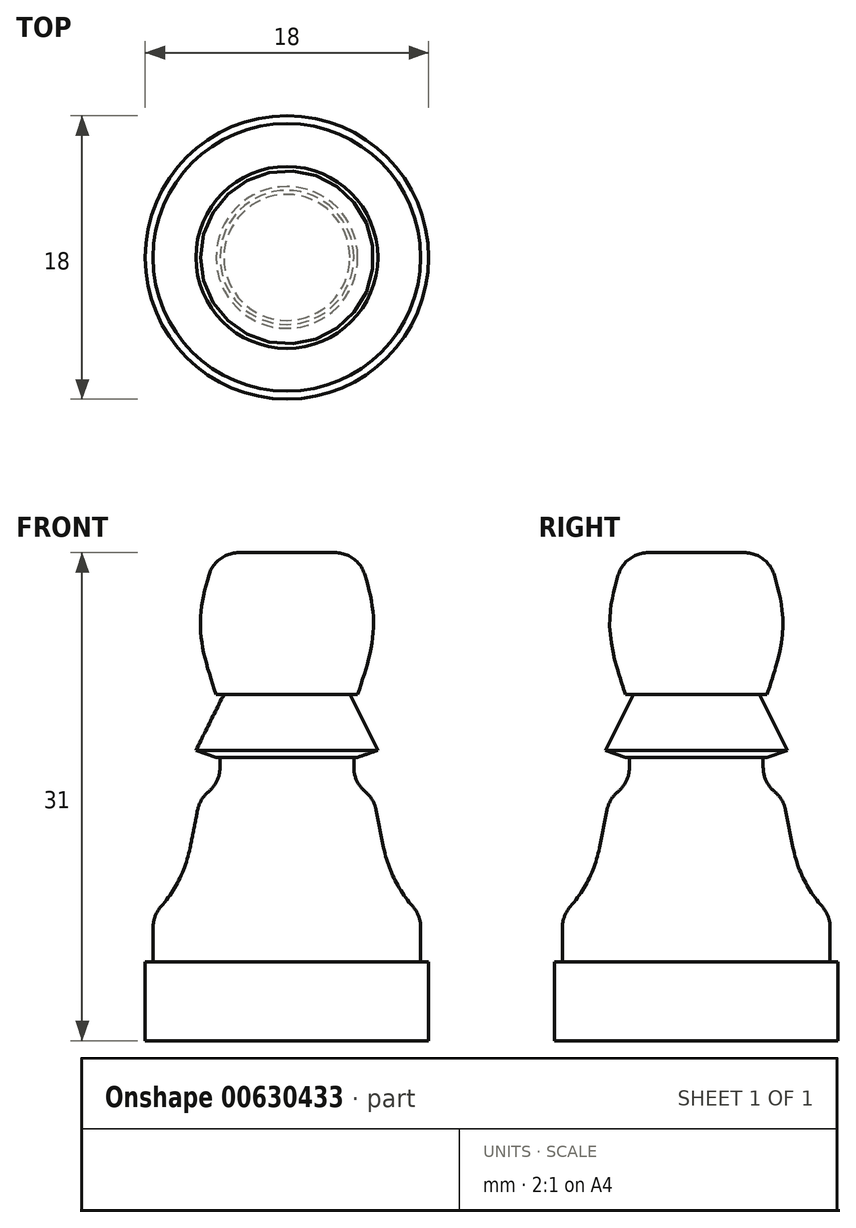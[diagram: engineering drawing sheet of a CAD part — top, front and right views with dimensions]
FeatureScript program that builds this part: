
annotation { "Feature Type Name" : "Feature", "Feature Type Description" : "" }
export const myFeature = defineFeature(function(context is Context, id is Id, definition is map)
    precondition{}
    {
        {
            var Q0;
            Q0=qCreatedBy(makeId("Front.planeOp"),FACE);
            var sketch = newSketch(context, id + "F0", { "sketchPlane" : qUnion([Q0])});
            skLineSegment(sketch, "E0", {"start": v(0, 0) * mm, "end": v(9, 0) * mm});
            skLineSegment(sketch, "E1", {"start": v(0, 0) * mm, "end": v(0, 31) * mm});
            skLineSegment(sketch, "E2", {"start": v(6, 18) * mm, "end": v(4.25, 18) * mm});
            skLineSegment(sketch, "E3", {"start": v(4.25, 18) * mm, "end": v(4.25, 15.5) * mm});
            skPoint(sketch, "E4.orphan", {"position": v(0, 15.5) * mm});
            skLineSegment(sketch, "E5", {"start": v(9, 0) * mm, "end": v(9, 5) * mm});
            skLineSegment(sketch, "E6", {"start": v(9, 5) * mm, "end": v(8.5, 5) * mm});
            skLineSegment(sketch, "E7", {"start": v(8.5, 5) * mm, "end": v(8.5, 8) * mm});
            skLineSegment(sketch, "E8", {"start": v(8.5, 8) * mm, "end": v(7, 8) * mm});
            skLineSegment(sketch, "E9", {"start": v(0, 31) * mm, "end": v(4.5, 31) * mm});
            skFitSpline(sketch, "E10", {"points": [v(4.5, 31) * mm, v(5.5, 26.5) * mm, v(4.5, 22) * mm], "startDerivative": vector(3, -9) * mm, "endDerivative": vector(-3, -9) * mm});
            skLineSegment(sketch, "E11", {"start": v(4.25, 15.5) * mm, "end": v(5.5, 15.5) * mm});
            skLineSegment(sketch, "E12", {"start": v(7, 8) * mm, "end": v(5.5, 15.5) * mm});
            skLineSegment(sketch, "E13", {"start": v(4.5, 22) * mm, "end": v(4, 22) * mm});
            skLineSegment(sketch, "E14", {"start": v(6, 18) * mm, "end": v(4, 22) * mm});
            skSolve(sketch);
        }
        {
            var Q0;
            Q0 = qSketchRegion(id + "F0", true);
            var Q1;
            Q1=sQuery(id+"F0.wireOp",EDGE,"E1");
            revolve(context, id + "F1", {"entities" : qUnion([Q0]), "axis" : qUnion([Q1]), "revolveType" : RevolveType.FULL});
        }
        {
            var Q0;
            Q0=makeQuery(id+"F1.opRevolve","SWEPT_EDGE",EDGE,{"disambiguationData":[OSD([sQuery(id+"F0.wireOp",EDGE,"E3"),sQuery(id+"F0.wireOp",EDGE,"E11")])]});
            fillet(context, id + "F2", {"entities" : qUnion([Q0]), "radius" : 2 * mm, "tangentPropagation" : true, "allowEdgeOverflow" : false});
        }
        {
            var Q0;
            Q0=makeQuery(id+"F1.opRevolve","SWEPT_EDGE",EDGE,{"disambiguationData":[OSD([sQuery(id+"F0.wireOp",EDGE,"E8"),sQuery(id+"F0.wireOp",EDGE,"E12")])]});
            fillet(context, id + "F3", {"entities" : qUnion([Q0]), "radius" : 8 * mm, "tangentPropagation" : true, "allowEdgeOverflow" : false});
        }
        {
            var Q0;
            Q0=makeQuery(id+"F2.opFillet","BLEND_EDGE",EDGE,{"blendedFrom":[makeQuery(id+"F1.opRevolve","SWEPT_EDGE",EDGE,{"disambiguationData":[OSD([sQuery(id+"F0.wireOp",EDGE,"E3"),sQuery(id+"F0.wireOp",EDGE,"E11")])]}),makeQuery(id+"F1.opRevolve","SWEPT_FACE",FACE,{"disambiguationData":[OSD([sQuery(id+"F0.wireOp",EDGE,"E12")])]})],"blendedInto":[makeQuery(id+"F1.opRevolve","SWEPT_FACE",FACE,{"disambiguationData":[OSD([sQuery(id+"F0.wireOp",EDGE,"E12")])]})]});
            fillet(context, id + "F4", {"entities" : qUnion([Q0]), "radius" : 2 * mm, "tangentPropagation" : true, "allowEdgeOverflow" : false});
        }
        {
            var Q0;
            Q0=makeQuery(id+"F3.opFillet","BLEND_EDGE",EDGE,{"blendedFrom":[makeQuery(id+"F1.opRevolve","SWEPT_EDGE",EDGE,{"disambiguationData":[OSD([sQuery(id+"F0.wireOp",EDGE,"E8"),sQuery(id+"F0.wireOp",EDGE,"E12")])]}),makeQuery(id+"F1.opRevolve","SWEPT_FACE",FACE,{"disambiguationData":[OSD([sQuery(id+"F0.wireOp",EDGE,"E7")])]})],"blendedInto":[makeQuery(id+"F1.opRevolve","SWEPT_FACE",FACE,{"disambiguationData":[OSD([sQuery(id+"F0.wireOp",EDGE,"E7")])]})]});
            fillet(context, id + "F5", {"entities" : qUnion([Q0]), "radius" : 2 * mm, "tangentPropagation" : true, "allowEdgeOverflow" : false});
        }
        {
            var Q0;
            Q0=makeQuery(id+"F1.opRevolve","SWEPT_EDGE",EDGE,{"disambiguationData":[OSD([sQuery(id+"F0.wireOp",EDGE,"E9"),sQuery(id+"F0.wireOp",EDGE,"E10")])]});
            fillet(context, id + "F6", {"entities" : qUnion([Q0]), "radius" : 2 * mm, "tangentPropagation" : true, "allowEdgeOverflow" : false});
        }
        {
            var Q0;
            Q0=makeQuery(id+"F1.opRevolve","SWEPT_EDGE",EDGE,{"disambiguationData":[OSD([sQuery(id+"F0.wireOp",EDGE,"E2"),sQuery(id+"F0.wireOp",EDGE,"E14")])]});
            chamfer(context, id + "F7", {"entities" : qUnion([Q0]), "chamferType" : ChamferType.TWO_OFFSETS, "width1" : 1.5 * mm, "oppositeDirection" : false, "width2" : .5 * mm, "tangentPropagation" : true});
        }
    });
